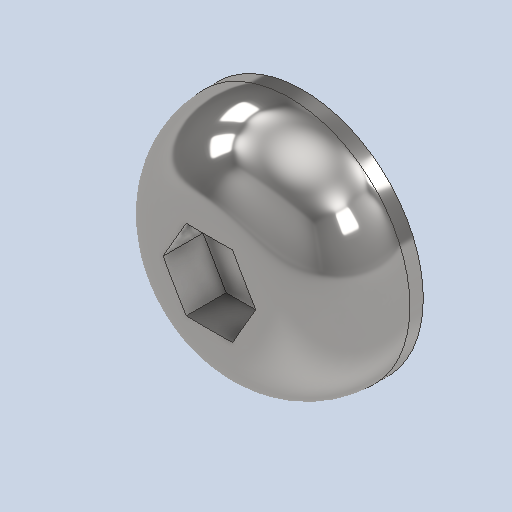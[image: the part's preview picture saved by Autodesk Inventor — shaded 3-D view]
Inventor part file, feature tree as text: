
AUTODESK INVENTOR PART (.ipt)
format: ipt  version: 2022 (Build 260153070, 153G)  size: 181,760 bytes
history: native  units: in
note: dims shown in document units (in); Inventor stores cm internally (conversion verified against a paired STEP export)
features: extrude x2, sketch x2, fillet x1
ambient origin geometry x8: Origin, YZ Plane, XZ Plane, XY Plane, X Axis, Y Axis, Z Axis, Center Point
bodies: Solid1 (feature_tree)
feature tree (5):
  extrude  "Extrusion1"  Depth=0.1181in TaperAngle=0.0deg
  fillet  "Fillet1"  Radius=0.1181in
  extrude  "Extrusion2"  Depth=0.1181in TaperAngle=0.0deg
  sketch  "Sketch1"  dims[d0=0.3543in d1=0.1378in d2=0.0in d3=0.1181in]
  sketch  "Sketch2"  dims[d4=0.1181in d5=0.0591in d6=0.0in]
